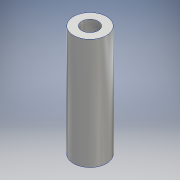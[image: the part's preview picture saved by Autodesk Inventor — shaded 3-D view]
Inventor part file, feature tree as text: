
AUTODESK INVENTOR PART (.ipt)
format: ipt  version: 2016 (Build 200138000, 138)  size: 111,104 bytes
history: native  units: mm
features: other x3, sketch x3, extrude x3, hole x2
ambient origin geometry x8: Origin, YZ Plane, XZ Plane, XY Plane, X Axis, Y Axis, Z Axis, Center Point
bodies: Body1 (feature_tree)
feature tree (11):
  other  "ソリッド1"
  sketch  "スケッチ1"
  extrude  "押し出し1"  Depth=8.0mm
  sketch  "スケッチ2"
  extrude  "押し出し2"  Depth=4.001mm
  hole  "穴1"  [1 undecoded]
  hole  "穴2"  [1 undecoded]
  other  "作業平面1"
  extrude  "押し出し3"  Depth=25.0mm TaperAngle=0.0deg
  sketch  "スケッチ3"
  other  "断面エッジを投影1"
note: 2 required parameter values undecoded (feature->parameter linkage not recoverable at this tier; creation-order binding heuristic only, values carry confidence <= 0.55)
